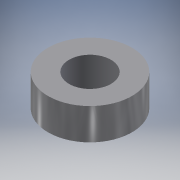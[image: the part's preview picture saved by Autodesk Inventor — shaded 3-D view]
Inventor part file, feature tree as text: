
AUTODESK INVENTOR PART (.ipt)
format: ipt  version: 2019 (Build 230136000, 136)  size: 102,912 bytes
history: native  units: in
note: dims shown in document units (in); Inventor stores cm internally (conversion verified against a paired STEP export)
features: extrude x1, sketch x1
ambient origin geometry x8: Origin, YZ Plane, XZ Plane, XY Plane, X Axis, Y Axis, Z Axis, Center Point
bodies: Solid1 (feature_tree)
feature tree (2):
  extrude  "Extrusion1"  Depth=0.1875in
  sketch  "Sketch1"  dims[d0=0.25in d1=0.5in d2=0.1875in d3=0.0in]
